# Revit family: Mirror-RectangularMirror-60cm-Vitra-İntegraSeries-62341
name_source: partatom
category: Furniture Systems
revit_build: Autodesk Revit 2017 (Build: 20160225_1515(x64)
units: mm (PartAtom-declared; Revit-internal decimal feet)

## family parameters
Cut with Voids When Loaded = No
Host = Face
OmniClass Number = 23.40.00.00
OmniClass Title = Equipment and Furnishings
Part Type = Normal
Room Calculation Point = No
Round Connector Dimension = Use Diameter
Shared = Yes

## types (2) — shared parameters
BIMobject category = Mirrors
Construction Type = Face Mounted
Default Elevation = 888 mm
Depth(mm) = 20 mm  [stored 0.0656168 ft]
Description = İntegra Mirror
Design country = Turkey
Height(mm) = 1072 mm
IFC Classification = Furniture
Manufacturer = Vitra
Manufacturer name = Vitra
Masterformat 2014 Code = 08 83 00
Masterformat 2014 Description = Mirrors
Nominal height = 0.000
Nominal width = 0.000
OmniClass Code = 23-21 00 00
OmniClass Description = Furnishings, Fixtures and Equipment Products
Primary Material = Mirror
Product certification = https://vitraglobal.com
Product data url = https://www.vitra-bad.fr
Product family = İntegra
Product group = Mirror
Technical description = http://cdn.vitra.com.tr
UNSPSC Code = 56
UNSPSC Description = Mirrors
URL = https://vitraglobal.com
Uniclass 1.4 Code = L8732
Uniclass 1.4 Description = Mirrors
Uniclass 2.0 Code = PR-71-55
Uniclass 2.0 Description = Mirrors
Uniclass 2015 Code = Pr_25_71_53
Uniclass 2015 Name = Mirrors
Uniformat II Code = E20
Uniformat II Description = FURNISHINGS
Warranty Period (Year) = 2
Youtube = https://www.youtube.com

## per-type parameters (varying)
| type | Article No. (default) | Model | Product SKU | Weight Net (kg) | Width(mm) |
| Mirror-60cm-Vitra-İntegra_62341 | 62341 | 62341 | 62341 | 8,5 | 566 mm  [stored 1.85696 ft] |
| Mirror-80cm-Vitra-İntegra_62342 | 62342 | 62342 | 62342 | 11 | 766 mm  [stored 2.51312 ft] |

note: [stored X ft] marks values corroborated as IEEE doubles in the binary element streams (Revit-internal decimal feet)

## geometry (parser evidence)
native form markers: Sweep x3
no freeform markers — native parametric forms only
